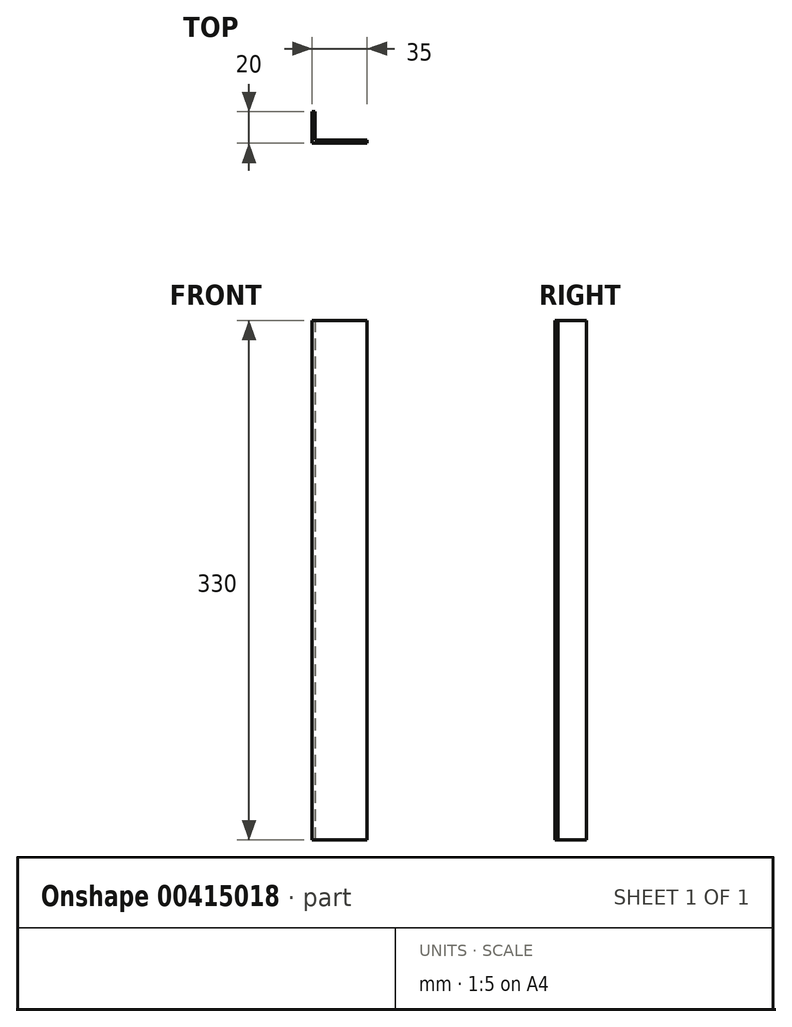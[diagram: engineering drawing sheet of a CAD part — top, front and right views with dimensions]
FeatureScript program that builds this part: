
annotation { "Feature Type Name" : "Feature", "Feature Type Description" : "" }
export const myFeature = defineFeature(function(context is Context, id is Id, definition is map)
    precondition{}
    {
        {
            var Q0;
            Q0=qCreatedBy(makeId("Top.planeOp"),FACE);
            var sketch = newSketch(context, id + "F0", { "sketchPlane" : qUnion([Q0])});
            skLineSegment(sketch, "E0", {"start": v(0, 20) * mm, "end": v(0, 0) * mm});
            skLineSegment(sketch, "E1", {"start": v(0, 0) * mm, "end": v(35, 0) * mm});
            skLineSegment(sketch, "E2", {"start": v(35, 0) * mm, "end": v(35, 2) * mm});
            skLineSegment(sketch, "E3", {"start": v(35, 2) * mm, "end": v(2, 2) * mm});
            skLineSegment(sketch, "E4", {"start": v(2, 2) * mm, "end": v(2, 20) * mm});
            skLineSegment(sketch, "E5", {"start": v(2, 20) * mm, "end": v(0, 20) * mm});
            skSolve(sketch);
        }
        {
            var Q0;
            Q0=makeQuery(id+"F0.imprint","IMPRINT",FACE,{"disambiguationData":[TD([[makeQuery(id+"F0.imprint","IMPRINT",EDGE,{"derivedFrom":sQuery(id+"F0.wireOp",EDGE,"E0")}),1.0]])]});
            extrude(context, id + "F1", {"entities" : qUnion([Q0]), "depth" : 330 * mm});
        }
    });
